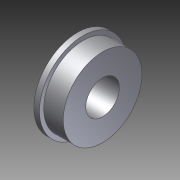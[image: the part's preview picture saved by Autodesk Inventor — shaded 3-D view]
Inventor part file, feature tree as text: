
AUTODESK INVENTOR PART (.ipt)
format: ipt  version: 2014 SP1 (Build 180222100, 222)  size: 110,080 bytes
history: native  units: in
note: dims shown in document units (in); Inventor stores cm internally (conversion verified against a paired STEP export)
features: revolve x1, other x1, imported_body x1
ambient origin geometry x8: Origin, YZ Plane, XZ Plane, XY Plane, X Axis, Y Axis, Z Axis, Center Point
bodies: Body1 (feature_tree)
feature tree (3):
  revolve  "Revolve1"  [1 undecoded]
  other  "217-2733.ipt1"
  imported_body  "Base1"
note: 1 required parameter value undecoded (feature->parameter linkage not recoverable at this tier; creation-order binding heuristic only, values carry confidence <= 0.55)
